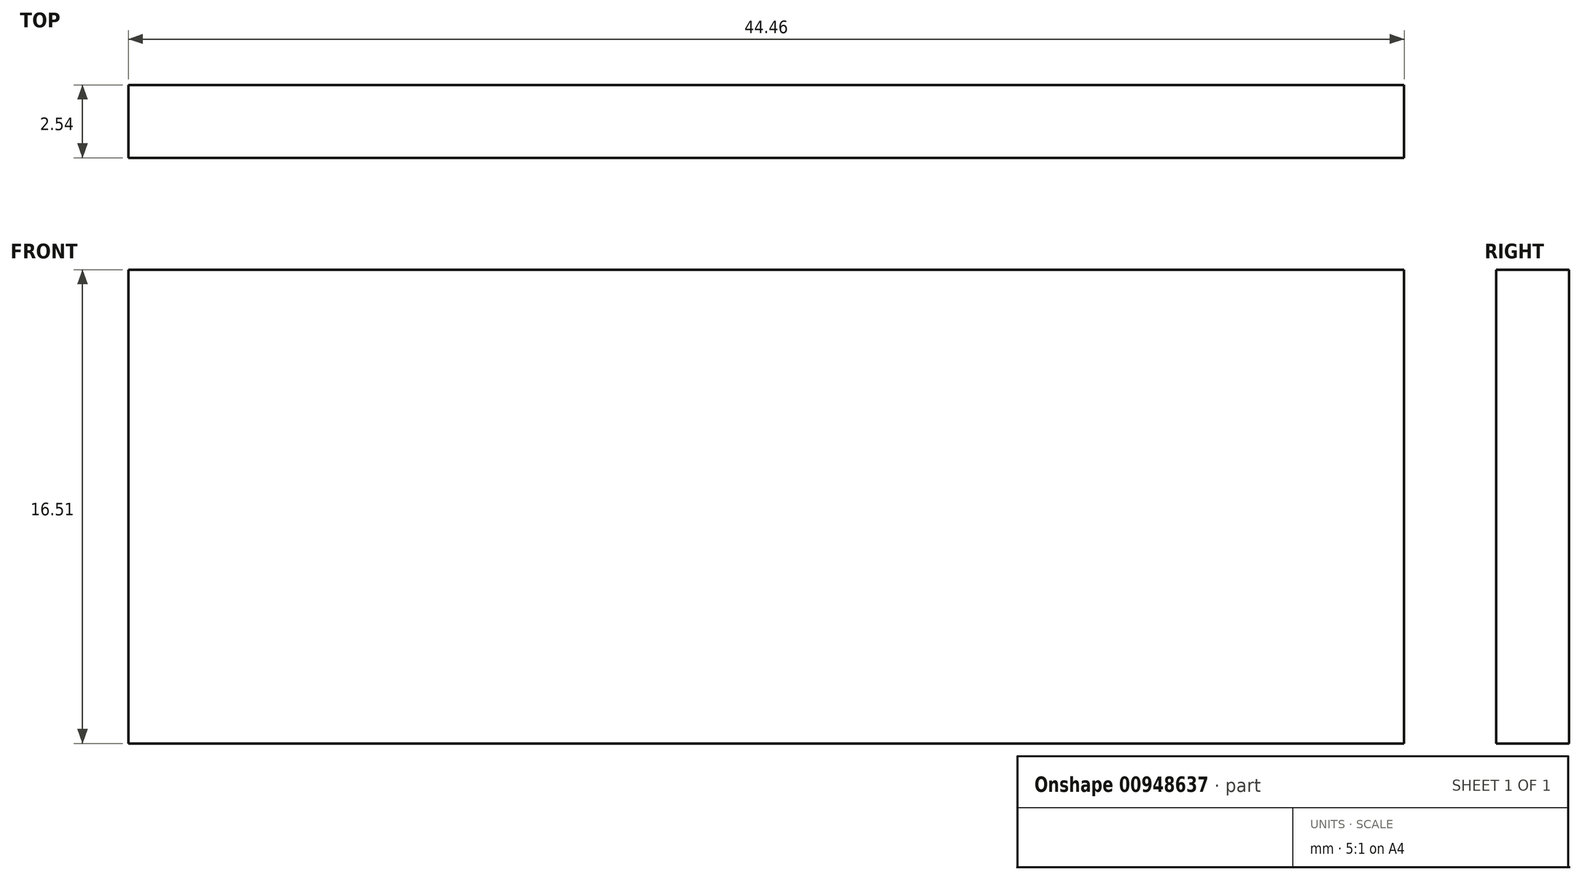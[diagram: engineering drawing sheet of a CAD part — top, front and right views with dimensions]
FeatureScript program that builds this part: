
annotation { "Feature Type Name" : "Feature", "Feature Type Description" : "" }
export const myFeature = defineFeature(function(context is Context, id is Id, definition is map)
    precondition{}
    {
        {
            var Q0;
            Q0=qCreatedBy(makeId("Top.planeOp"),FACE);
            var sketch = newSketch(context, id + "F0", { "sketchPlane" : qUnion([Q0])});
            skLineSegment(sketch, "E0.bottom", {"start": v(22.23, -1.27) * mm, "end": v(-22.23, -1.27) * mm});
            skLineSegment(sketch, "E0.top", {"start": v(22.23, 1.27) * mm, "end": v(-22.23, 1.27) * mm});
            skLineSegment(sketch, "E0.left", {"start": v(22.23, -1.27) * mm, "end": v(22.23, 1.27) * mm});
            skLineSegment(sketch, "E0.right", {"start": v(-22.23, -1.27) * mm, "end": v(-22.23, 1.27) * mm});
            skPoint(sketch, "E0.middle", {"position": v(0, 0) * mm});
            skSolve(sketch);
        }
        {
            var Q0;
            Q0=makeQuery(id+"F0.imprint","IMPRINT",FACE,{"disambiguationData":[TD([[makeQuery(id+"F0.imprint","IMPRINT",EDGE,{"derivedFrom":sQuery(id+"F0.wireOp",EDGE,"E0.bottom")}),-1.0]])]});
            extrude(context, id + "F1", {"entities" : qUnion([Q0]), "depth" : 16.5 * mm, "offsetDistance" : 25.4 * mm});
        }
    });
